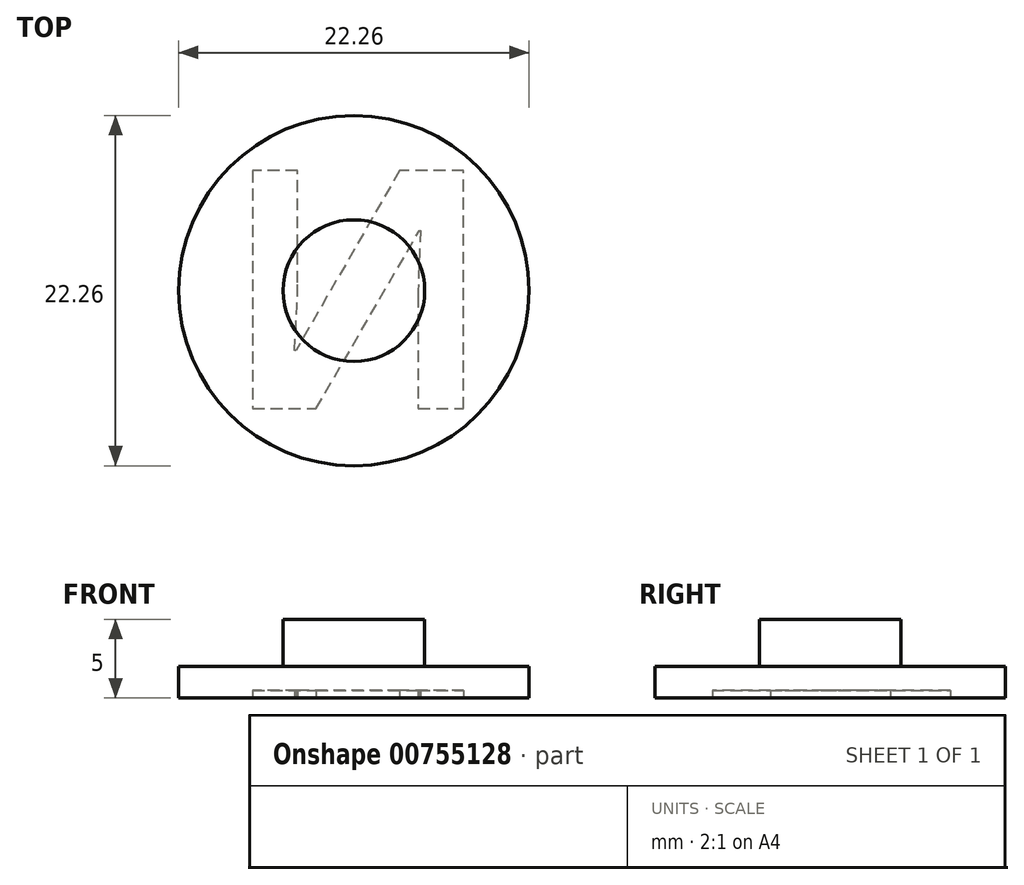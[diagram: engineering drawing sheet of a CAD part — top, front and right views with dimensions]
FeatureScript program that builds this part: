
annotation { "Feature Type Name" : "Feature", "Feature Type Description" : "" }
export const myFeature = defineFeature(function(context is Context, id is Id, definition is map)
    precondition{}
    {
        {
            var Q0;
            Q0=qCreatedBy(makeId("Top.planeOp"),FACE);
            var sketch = newSketch(context, id + "F0", { "sketchPlane" : qUnion([Q0])});
            skCircle(sketch, "E0", {"center": v(0, 0) * mm, "radius": 4.5 * mm});
            skSolve(sketch);
        }
        {
            var Q0;
            Q0=makeQuery(id+"F0.imprint","IMPRINT",FACE,{"disambiguationData":[TD([[makeQuery(id+"F0.imprint","IMPRINT",EDGE,{"derivedFrom":sQuery(id+"F0.wireOp",EDGE,"E0")}),1.0]])]});
            extrude(context, id + "F1", {"entities" : qUnion([Q0]), "depth" : 3 * mm, "offsetDistance" : 25.4 * mm});
        }
        {
            var Q0;
            Q0=qCreatedBy(makeId("Top.planeOp"),FACE);
            var sketch = newSketch(context, id + "F2", { "sketchPlane" : qUnion([Q0])});
            skCircle(sketch, "E1", {"center": v(0, 0) * mm, "radius": 11.12 * mm});
            skSolve(sketch);
        }
        {
            var Q0;
            Q0=makeQuery(id+"F2.imprint","IMPRINT",FACE,{"disambiguationData":[TD([[makeQuery(id+"F2.imprint","IMPRINT",EDGE,{"derivedFrom":sQuery(id+"F2.wireOp",EDGE,"E1")}),1.0]])]});
            extrude(context, id + "F3", {"entities" : qUnion([Q0]), "operationType" : NewBodyOperationType.ADD, "oppositeDirection" : true, "depth" : 2 * mm, "offsetDistance" : 25.4 * mm});
        }
        {
            var Q0;
            Q0=makeQuery(id+"F3.opExtrude","CAP_FACE",FACE,{"disambiguationData":[OSD([sQuery(id+"F2.wireOp",EDGE,"E1")])],"isStart":false});
            var sketch = newSketch(context, id + "F4", { "sketchPlane" : qUnion([Q0])});
            skText(sketch, "E2", { "text": "N", "fontName": "OpenSans-Bold.ttf"});
            skLineSegment(sketch, "E3", {"start": v(-8.34, 7.62) * mm, "end": v(8.34, -7.62) * mm, "construction": true});
            skLineSegment(sketch, "E4", {"start": v(8.34, 7.62) * mm, "end": v(-8.34, -7.62) * mm, "construction": true});
            skPoint(sketch, "E5", {"position": v(0, 0) * mm});
            const initialGuessF4  = {"E2": [-0.00834, -0.00762, 1, 0, 0.01524]};
            skSetInitialGuess(sketch, initialGuessF4);
            skSolve(sketch);
        }
        {
            var Q0;
            Q0=qSketchRegion(id+"F4",true);
            extrude(context, id + "F5", {"entities" : qUnion([Q0]), "operationType" : NewBodyOperationType.REMOVE, "oppositeDirection" : true, "depth" : .5 * mm, "offsetDistance" : 25.4 * mm});
        }
    });
